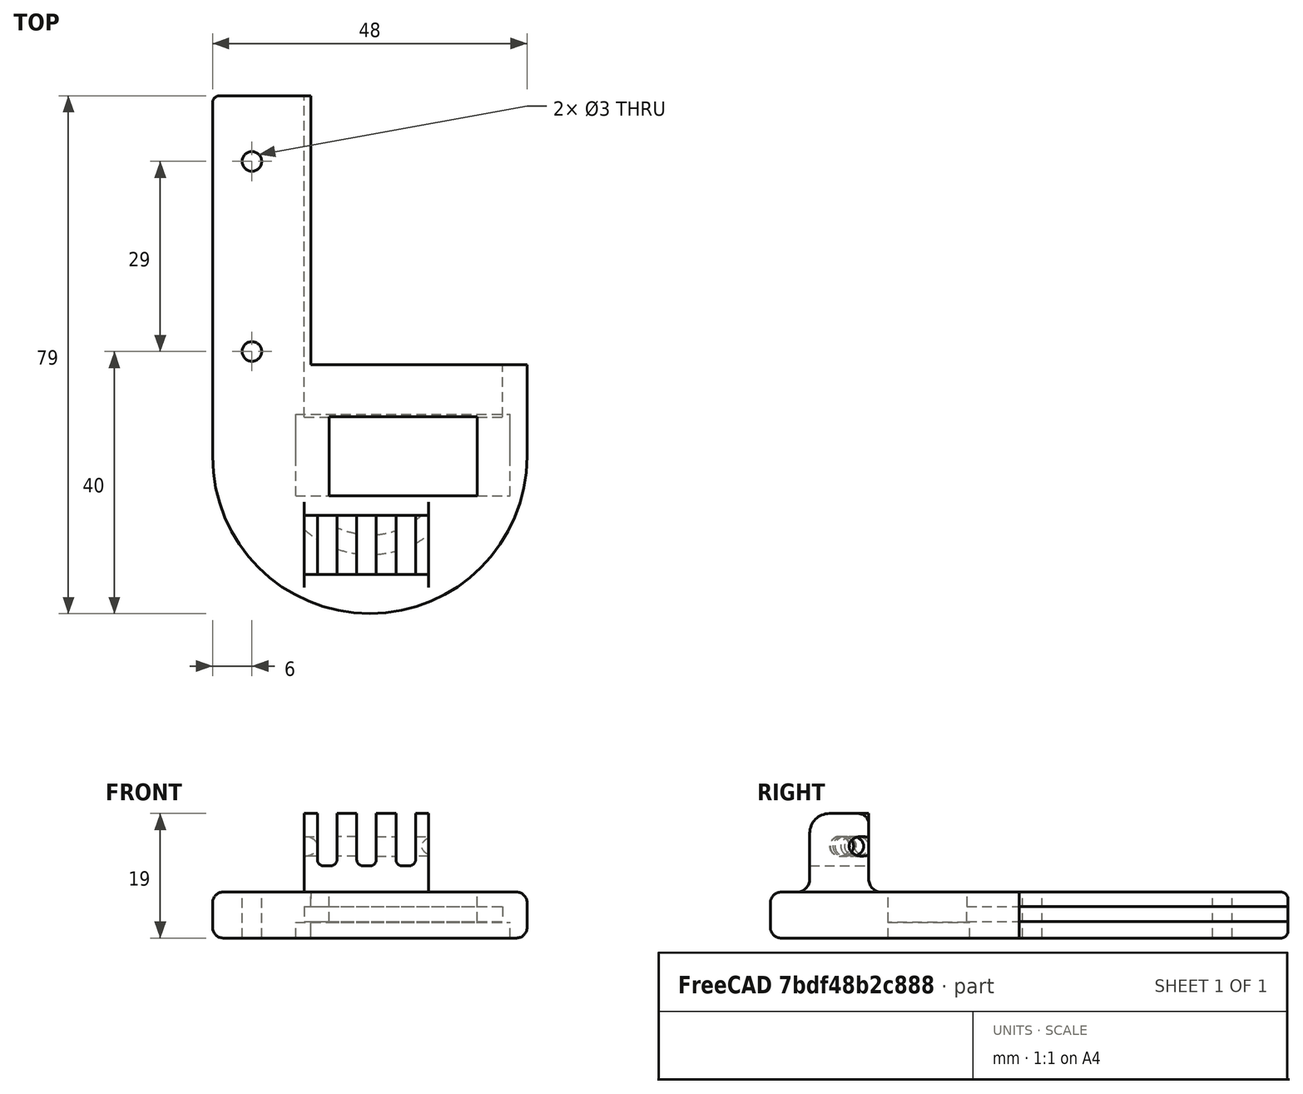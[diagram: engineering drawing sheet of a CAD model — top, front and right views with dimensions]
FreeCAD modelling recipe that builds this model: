
FCSTD DOCUMENT  (FreeCAD 0.18R16110 (Git))
Label: beardropper
License: All rights reserved
LicenseURL: http://en.wikipedia.org/wiki/All_rights_reserved
objects: Part::Box×9, Part::Cylinder×4, Part::MultiFuse×2, Part::Torus×1, Part::Cut×1, Part::Fillet×1
note: 18 computed .brp shape members not serialized (recipe doc carries the construction recipe); baked Part::Feature solids carry a one-line shape summary decoded from their .brp

FEATURE [Part::Cylinder] Cylinder
  Angle = 360
  AttacherType = Attacher::AttachEngine3D
  Height = 10
  Radius = 2.5
FEATURE [Part::Box] Box  label="Cube"
  AttacherType = Attacher::AttachEngine3D
  Height = 27
  Length = 22.6
  Placement = pos=(-6.2,-6.05,-20) rot=(0,0,1;0rad)
  Width = 12.1
FEATURE [Part::Box] Box001  label="Cube001"
  AttacherType = Attacher::AttachEngine3D
  Height = 2.4
  Length = 32.7
  Placement = pos=(-11.3,-6.05,-4) rot=(0,0,1;0rad)
  Width = 12.5
FEATURE [Part::Box] Box002  label="Cube002"
  AttacherType = Attacher::AttachEngine3D
  Height = 7
  Length = 48
  Placement = pos=(-24,0,-4) rot=(0,0,1;0rad)
  Width = 14
FEATURE [Part::Box] Box003  label="Cube003"
  AttacherType = Attacher::AttachEngine3D
  Height = 2.3
  Length = 30.3
  Placement = pos=(-10,6,-1.5) rot=(0,0,1;0rad)
  Width = 80
FEATURE [Part::Torus] Torus
  Angle1 = -180
  Angle2 = 180
  Angle3 = 360
  AttacherType = Attacher::AttachEngine3D
  Placement = pos=(0,0,10) rot=(0,0,1;0rad)
  Radius1 = 13.5
  Radius2 = 1.5
FEATURE [Part::Cylinder] Cylinder001
  Angle = 180
  AttacherType = Attacher::AttachEngine3D
  Height = 7
  Placement = pos=(0,0,-4) rot=(0,0,1;3.14159rad)
  Radius = 24
FEATURE [Part::Box] Box004  label="Cube004"
  AttacherType = Attacher::AttachEngine3D
  Height = 15
  Length = 19
  Placement = pos=(-10,-18,0) rot=(0,0,1;0rad)
  Width = 9
FEATURE [Part::Box] Box005  label="Cube005"
  AttacherType = Attacher::AttachEngine3D
  Height = 19
  Length = 3
  Placement = pos=(-8,-23,7) rot=(0,0,1;0rad)
  Width = 19
FEATURE [Part::Box] Box006  label="Cube006"
  AttacherType = Attacher::AttachEngine3D
  Height = 19
  Length = 3
  Placement = pos=(-2,-23,7) rot=(0,0,1;0rad)
  Width = 19
FEATURE [Part::Box] Box007  label="Cube007"
  AttacherType = Attacher::AttachEngine3D
  Height = 19
  Length = 3
  Placement = pos=(4,-23,7) rot=(0,0,1;0rad)
  Width = 19
FEATURE [Part::Cylinder] Cylinder002
  Angle = 360
  AttacherType = Attacher::AttachEngine3D
  Height = 10
  Placement = pos=(-18,45,-6) rot=(0,0,1;0rad)
  Radius = 1.5
FEATURE [Part::Cylinder] Cylinder003
  Angle = 360
  AttacherType = Attacher::AttachEngine3D
  Height = 10
  Placement = pos=(-18,16,-6) rot=(0,0,1;0rad)
  Radius = 1.5
FEATURE [Part::Box] Box008  label="Cube008"
  AttacherType = Attacher::AttachEngine3D
  Height = 7
  Length = 15
  Placement = pos=(-24,0,-4) rot=(0,0,1;0rad)
  Width = 55
FEATURE [Part::MultiFuse] Fusion001
  Shapes = -> [Cylinder001,Box004,Box008,Box002]
FEATURE [Part::MultiFuse] Fusion
  Shapes = -> [Cylinder002,Cylinder003,Torus,Box005,Box007,Cylinder,Box,Box003,Box001,Box006]
FEATURE [Part::Cut] Cut
  Base = -> Fusion001
  Tool = -> Fusion
FEATURE [Part::Fillet] Fillet
  Base = -> Cut
  Edges = 22 edges: [Edge1 r=1.6,Edge11 r=2,Edge14 r=2,Edge15 r=1.6,Edge25 r=1.6,Edge50 r=3,Edge54 r=3,Edge58 r=3,Edge62 r=3,Edge75 r=1.6,Edge79 r=1.6,Edge83 r=1.6,Edge111 r=1,Edge112 r=1.6,Edge113 r=1,Edge136 r=1,Edge138 r=1,Edge142 r=1,Edge144 r=1,Edge148 r=1,Edge150 r=1,Edge162 r=1]
